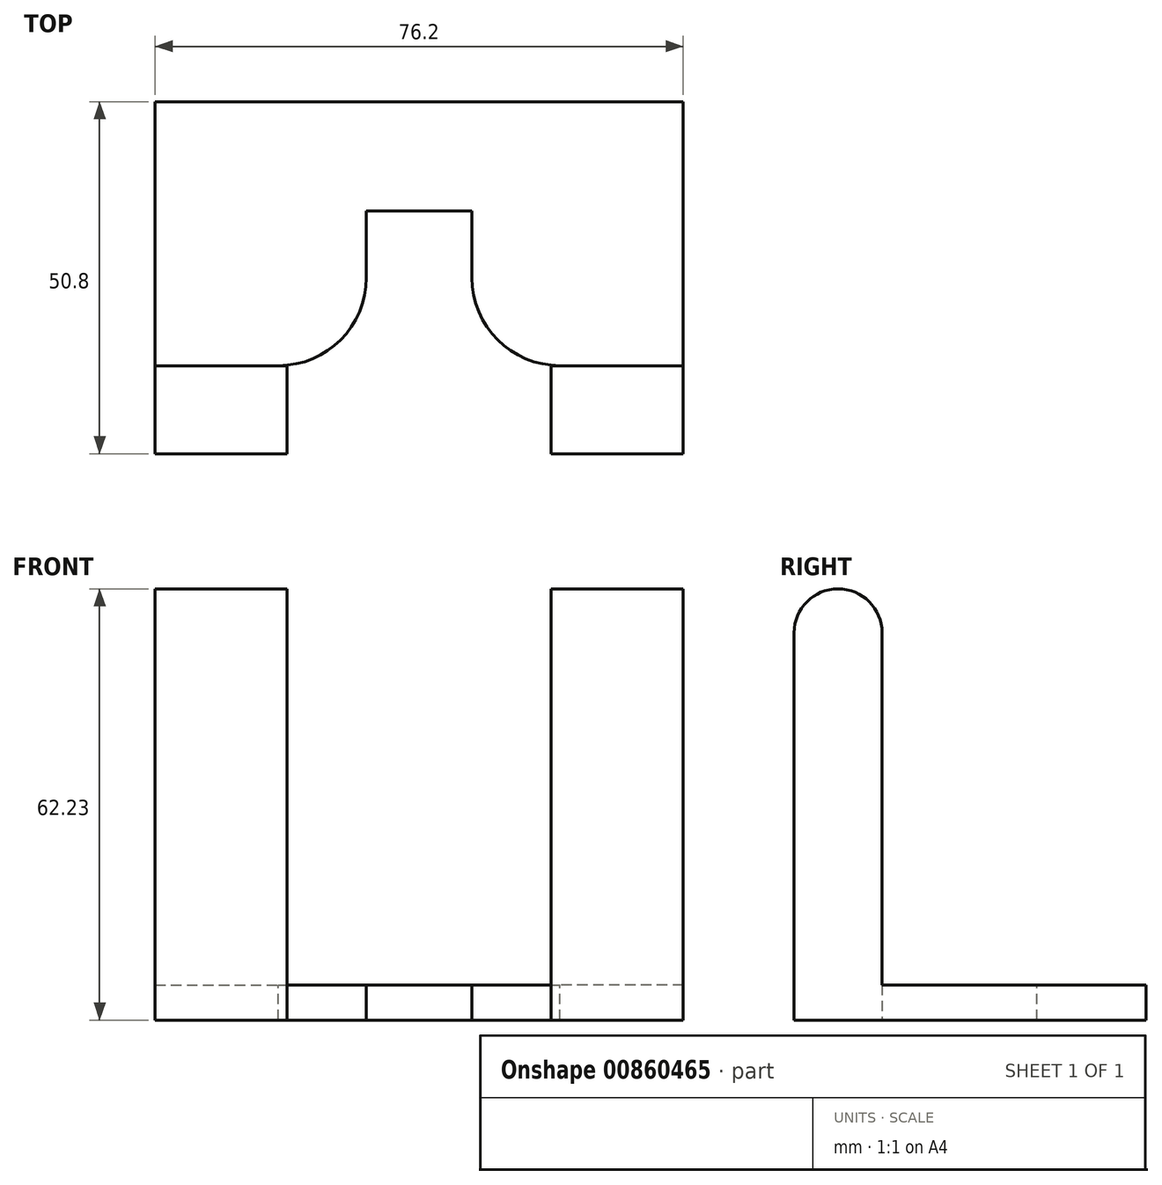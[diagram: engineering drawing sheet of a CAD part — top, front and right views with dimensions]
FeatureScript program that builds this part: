
annotation { "Feature Type Name" : "Feature", "Feature Type Description" : "" }
export const myFeature = defineFeature(function(context is Context, id is Id, definition is map)
    precondition{}
    {
        {
            var Q0;
            Q0=qCreatedBy(makeId("Top.planeOp"),FACE);
            var sketch = newSketch(context, id + "F0", { "sketchPlane" : qUnion([Q0])});
            skLineSegment(sketch, "E0.bottom", {"start": v(0, 0) * mm, "end": v(76.2, 0) * mm});
            skLineSegment(sketch, "E0.top", {"start": v(0, 50.8) * mm, "end": v(76.2, 50.8) * mm});
            skLineSegment(sketch, "E0.left", {"start": v(0, 0) * mm, "end": v(0, 50.8) * mm});
            skLineSegment(sketch, "E0.right", {"start": v(76.2, 0) * mm, "end": v(76.2, 50.8) * mm});
            skLineSegment(sketch, "E1.bottom", {"start": v(0, 0) * mm, "end": v(19.05, 0) * mm});
            skLineSegment(sketch, "E1.left", {"start": v(0, 0) * mm, "end": v(0, 12.7) * mm});
            skSolve(sketch);
        }
        {
            var Q0;
            Q0=makeQuery(id+"F0.imprint","IMPRINT",FACE,{"disambiguationData":[TD([[makeQuery(id+"F0.imprint","IMPRINT",EDGE,{"derivedFrom":sQuery(id+"F0.wireOp",EDGE,"E0.bottom")}),1.0]])]});
            extrude(context, id + "F1", {"entities" : qUnion([Q0]), "depth" : 5.08 * mm, "offsetDistance" : 25.4 * mm});
        }
        {
            var Q0;
            Q0=makeQuery(id+"F1.opExtrude","CAP_FACE",FACE,{"disambiguationData":[OSD([sQuery(id+"F0.wireOp",EDGE,"E0.bottom"),sQuery(id+"F0.wireOp",EDGE,"E0.top"),sQuery(id+"F0.wireOp",EDGE,"E0.left"),sQuery(id+"F0.wireOp",EDGE,"E0.right"),sQuery(id+"F0.wireOp",EDGE,"E1.bottom"),sQuery(id+"F0.wireOp",EDGE,"E1.left")])],"isStart":false});
            var sketch = newSketch(context, id + "F2", { "sketchPlane" : qUnion([Q0])});
            skLineSegment(sketch, "E2.bottom", {"start": v(0, 0) * mm, "end": v(19.05, 0) * mm});
            skLineSegment(sketch, "E2.top", {"start": v(0, 12.7) * mm, "end": v(19.05, 12.7) * mm});
            skLineSegment(sketch, "E2.left", {"start": v(0, 0) * mm, "end": v(0, 12.7) * mm});
            skLineSegment(sketch, "E2.right", {"start": v(19.05, 0) * mm, "end": v(19.05, 12.7) * mm});
            skLineSegment(sketch, "E3.bottom", {"start": v(76.2, 0) * mm, "end": v(57.15, 0) * mm});
            skLineSegment(sketch, "E3.top", {"start": v(76.2, 12.7) * mm, "end": v(57.15, 12.7) * mm});
            skLineSegment(sketch, "E3.left", {"start": v(76.2, 0) * mm, "end": v(76.2, 12.7) * mm});
            skLineSegment(sketch, "E3.right", {"start": v(57.15, 0) * mm, "end": v(57.15, 12.7) * mm});
            skSolve(sketch);
        }
        {
            var Q0;
            Q0=makeQuery(id+"F2.imprint","IMPRINT",FACE,{"disambiguationData":[TD([[makeQuery(id+"F2.imprint","IMPRINT",EDGE,{"derivedFrom":sQuery(id+"F2.wireOp",EDGE,"E2.bottom")}),1.0]])]});
            var Q1;
            Q1=makeQuery(id+"F2.imprint","IMPRINT",FACE,{"disambiguationData":[TD([[makeQuery(id+"F2.imprint","IMPRINT",EDGE,{"derivedFrom":sQuery(id+"F2.wireOp",EDGE,"E3.bottom")}),1.0]])]});
            extrude(context, id + "F3", {"entities" : qUnion([Q0, Q1]), "operationType" : NewBodyOperationType.ADD, "depth" : 50.8 * mm, "offsetDistance" : 25.4 * mm});
        }
        {
            var Q0;
            Q0=makeQuery(id+"F3.boolean.opBoolean","MERGE",FACE,{"derivedFrom":[makeQuery(id+"F1.opExtrude","SWEPT_FACE",FACE,{"disambiguationData":[OSD([sQuery(id+"F0.wireOp",EDGE,"E0.left"),sQuery(id+"F0.wireOp",EDGE,"E1.left")])]}),makeQuery(id+"F3.opExtrude","SWEPT_FACE",FACE,{"disambiguationData":[OSD([sQuery(id+"F2.wireOp",EDGE,"E2.left")])]})]});
            var sketch = newSketch(context, id + "F4", { "sketchPlane" : qUnion([Q0])});
            skCircle(sketch, "E4", {"center": v(-6.35, 55.88) * mm, "radius": 6.35 * mm});
            skSolve(sketch);
        }
        {
            var Q0;
            {var subQ1=sQuery(id+"F2.wireOp",EDGE,"E2.left");var subQ3=makeQuery(id+"F3.opExtrude","CAP_EDGE",EDGE,{"disambiguationData":[OSD([subQ1])],"isStart":false});Q0=makeQuery(id+"F4.imprint","IMPRINT",FACE,{"disambiguationData":[TD([[makeQuery(id+"F4.imprint","IMPRINT",EDGE,{"derivedFrom":subQ3}),-1.0]])]});}
            var Q1;
            {var subQ1=sQuery(id+"F2.wireOp",EDGE,"E2.left");var subQ3=makeQuery(id+"F3.opExtrude","CAP_EDGE",EDGE,{"disambiguationData":[OSD([subQ1])],"isStart":false});Q1=makeQuery(id+"F4.imprint","IMPRINT",FACE,{"disambiguationData":[TD([[makeQuery(id+"F4.imprint","IMPRINT",EDGE,{"derivedFrom":subQ3}),1.0]])]});}
            extrude(context, id + "F5", {"entities" : qUnion([Q0, Q1]), "operationType" : NewBodyOperationType.ADD, "oppositeDirection" : true, "depth" : 19.05 * mm, "offsetDistance" : 25.4 * mm});
        }
        {
            var Q0;
            Q0=makeQuery(id+"F3.boolean.opBoolean","MERGE",FACE,{"derivedFrom":[makeQuery(id+"F1.opExtrude","SWEPT_FACE",FACE,{"disambiguationData":[OSD([sQuery(id+"F0.wireOp",EDGE,"E0.right")])]}),makeQuery(id+"F3.opExtrude","SWEPT_FACE",FACE,{"disambiguationData":[OSD([sQuery(id+"F2.wireOp",EDGE,"E3.left")])]})]});
            var sketch = newSketch(context, id + "F6", { "sketchPlane" : qUnion([Q0])});
            skCircle(sketch, "E5", {"center": v(6.35, 55.88) * mm, "radius": 6.35 * mm});
            skSolve(sketch);
        }
        {
            var Q0;
            {var subQ1=sQuery(id+"F2.wireOp",EDGE,"E3.left");var subQ3=makeQuery(id+"F3.opExtrude","CAP_EDGE",EDGE,{"disambiguationData":[OSD([subQ1])],"isStart":false});Q0=makeQuery(id+"F6.imprint","IMPRINT",FACE,{"disambiguationData":[TD([[makeQuery(id+"F6.imprint","IMPRINT",EDGE,{"derivedFrom":subQ3}),1.0]])]});}
            var Q1;
            {var subQ1=sQuery(id+"F2.wireOp",EDGE,"E3.left");var subQ3=makeQuery(id+"F3.opExtrude","CAP_EDGE",EDGE,{"disambiguationData":[OSD([subQ1])],"isStart":false});Q1=makeQuery(id+"F6.imprint","IMPRINT",FACE,{"disambiguationData":[TD([[makeQuery(id+"F6.imprint","IMPRINT",EDGE,{"derivedFrom":subQ3}),-1.0]])]});}
            extrude(context, id + "F7", {"entities" : qUnion([Q0, Q1]), "operationType" : NewBodyOperationType.ADD, "oppositeDirection" : true, "depth" : 19.05 * mm, "offsetDistance" : 25.4 * mm});
        }
        {
            var Q0;
            Q0=makeQuery(id+"F1.opExtrude","CAP_FACE",FACE,{"disambiguationData":[OSD([sQuery(id+"F0.wireOp",EDGE,"E0.bottom"),sQuery(id+"F0.wireOp",EDGE,"E0.top"),sQuery(id+"F0.wireOp",EDGE,"E0.left"),sQuery(id+"F0.wireOp",EDGE,"E0.right"),sQuery(id+"F0.wireOp",EDGE,"E1.bottom"),sQuery(id+"F0.wireOp",EDGE,"E1.left")])],"isStart":false});
            var sketch = newSketch(context, id + "F8", { "sketchPlane" : qUnion([Q0])});
            skLineSegment(sketch, "E6.bottom", {"start": v(0, 12.7) * mm, "end": v(17.78, 12.7) * mm});
            skLineSegment(sketch, "E6.left", {"start": v(0, 12.7) * mm, "end": v(0, 35.05) * mm});
            skLineSegment(sketch, "E6.right", {"start": v(30.48, 25.4) * mm, "end": v(30.48, 35.05) * mm});
            skArc(sketch, "E7", {"start": v(17.78, 12.7) * mm, "mid": v(26.76, 16.42) * mm, "end": v(30.48, 25.4) * mm});
            skLineSegment(sketch, "E8.bottom", {"start": v(76.2, 12.7) * mm, "end": v(58.42, 12.7) * mm});
            skLineSegment(sketch, "E8.left", {"start": v(76.2, 12.7) * mm, "end": v(76.2, 35.05) * mm});
            skLineSegment(sketch, "E8.right", {"start": v(45.72, 25.4) * mm, "end": v(45.72, 35.05) * mm});
            skArc(sketch, "E9", {"start": v(45.72, 25.4) * mm, "mid": v(49.44, 16.42) * mm, "end": v(58.42, 12.7) * mm});
            skLineSegment(sketch, "E10.bottom", {"start": v(0, 50.8) * mm, "end": v(76.2, 50.8) * mm});
            skLineSegment(sketch, "E10.top", {"start": v(30.48, 35.05) * mm, "end": v(45.72, 35.05) * mm});
            skLineSegment(sketch, "E10.left", {"start": v(0, 50.8) * mm, "end": v(0, 35.05) * mm});
            skLineSegment(sketch, "E10.right", {"start": v(76.2, 50.8) * mm, "end": v(76.2, 35.05) * mm});
            skSolve(sketch);
        }
        {
            var Q0;
            Q0=makeQuery(id+"F8.imprint","IMPRINT",FACE,{"disambiguationData":[TD([[makeQuery(id+"F8.imprint","IMPRINT",EDGE,{"derivedFrom":sQuery(id+"F8.wireOp",EDGE,"E6.right")}),-1.0]])]});
            extrude(context, id + "F9", {"entities" : qUnion([Q0]), "operationType" : NewBodyOperationType.REMOVE, "oppositeDirection" : true, "depth" : 5.08 * mm, "offsetDistance" : 25.4 * mm});
        }
    });
